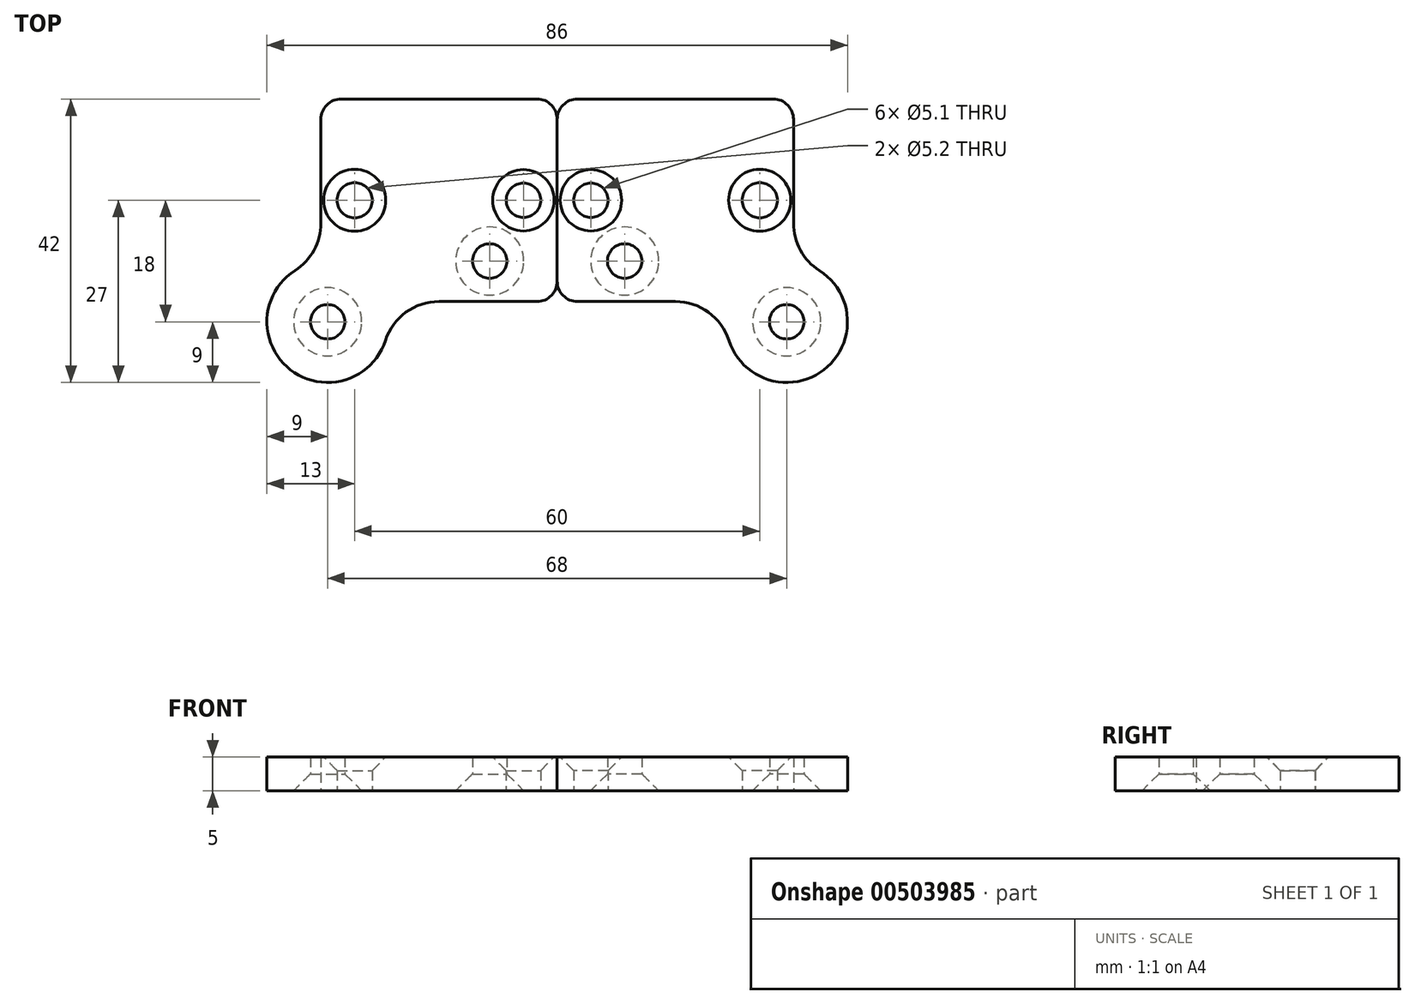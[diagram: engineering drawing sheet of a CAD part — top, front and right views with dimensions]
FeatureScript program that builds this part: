
annotation { "Feature Type Name" : "Feature", "Feature Type Description" : "" }
export const myFeature = defineFeature(function(context is Context, id is Id, definition is map)
    precondition{}
    {
        {
            var Q0;
            Q0=qCreatedBy(makeId("Top.planeOp"),FACE);
            var sketch = newSketch(context, id + "F0", { "sketchPlane" : qUnion([Q0])});
            skLineSegment(sketch, "E0", {"start": v(-17.5, -12) * mm, "end": v(-17.5, 12) * mm});
            skLineSegment(sketch, "E1", {"start": v(-14.5, 15) * mm, "end": v(14.5, 15) * mm});
            skCircle(sketch, "E2", {"center": v(-12.5, 0) * mm, "radius": 2.55 * mm});
            skLineSegment(sketch, "E3", {"start": v(-14.5, -15) * mm, "end": v(0, -15) * mm});
            skCircle(sketch, "E4", {"center": v(16.5, -18) * mm, "radius": 2.55 * mm});
            skLineSegment(sketch, "E5", {"start": v(-17.5, 0) * mm, "end": v(17.5, 0) * mm, "construction": true});
            skCircle(sketch, "E6", {"center": v(12.5, 0) * mm, "radius": 2.6 * mm});
            skLineSegment(sketch, "E7", {"start": v(0, 15) * mm, "end": v(0, -15) * mm, "construction": true});
            skPoint(sketch, "E8.visualSharp", {"position": v(-17.5, 15) * mm});
            skArc(sketch, "E8.filletArc", {"start": v(-14.5, 15) * mm, "mid": v(-16.62, 14.12) * mm, "end": v(-17.5, 12) * mm});
            skPoint(sketch, "E9.visualSharp", {"position": v(-17.5, -15) * mm});
            skArc(sketch, "E9.filletArc", {"start": v(-17.5, -12) * mm, "mid": v(-16.62, -14.12) * mm, "end": v(-14.5, -15) * mm});
            skCircle(sketch, "E10", {"center": v(-7.5, -9) * mm, "radius": 2.55 * mm});
            skLineSegment(sketch, "E11", {"start": v(17.5, 12) * mm, "end": v(17.5, -3.41) * mm});
            skCircle(sketch, "E12", {"center": v(16.5, -18) * mm, "radius": 9 * mm});
            skArc(sketch, "E13", {"start": v(7.94, -20.77) * mm, "mid": v(4.9, -16.6) * mm, "end": v(0, -15) * mm});
            skArc(sketch, "E14", {"start": v(17.5, -3.41) * mm, "mid": v(18.52, -7.4) * mm, "end": v(21.34, -10.41) * mm});
            skPoint(sketch, "E15.visualSharp", {"position": v(17.5, 15) * mm});
            skArc(sketch, "E15.filletArc", {"start": v(17.5, 12) * mm, "mid": v(16.62, 14.12) * mm, "end": v(14.5, 15) * mm});
            skSolve(sketch);
        }
        {
            var Q0;
            Q0=qSketchRegion(id+"F0",true);
            extrude(context, id + "F1", {"entities" : qUnion([Q0]), "depth" : 5 * mm, "offsetDistance" : 25 * mm});
        }
        {
            var Q0;
            Q0=makeQuery(id+"F1.opExtrude","CAP_EDGE",EDGE,{"disambiguationData":[OSD([sQuery(id+"F0.wireOp",EDGE,"E10")])],"isStart":true});
            chamfer(context, id + "F2", {"entities" : qUnion([Q0]), "width" : 2.5 * mm, "tangentPropagation" : true});
        }
        {
            var Q0;
            Q0=makeQuery(id+"F1.opExtrude","CAP_EDGE",EDGE,{"disambiguationData":[OSD([sQuery(id+"F0.wireOp",EDGE,"E6")])],"isStart":false});
            var Q1;
            Q1=makeQuery(id+"F1.opExtrude","CAP_EDGE",EDGE,{"disambiguationData":[OSD([sQuery(id+"F0.wireOp",EDGE,"E2")])],"isStart":false});
            chamfer(context, id + "F3", {"entities" : qUnion([Q0, Q1]), "width" : 2 * mm, "tangentPropagation" : true});
        }
        {
            var Q0;
            Q0=makeQuery(id+"F1.opExtrude","CAP_EDGE",EDGE,{"disambiguationData":[OSD([sQuery(id+"F0.wireOp",EDGE,"E4")])],"isStart":true});
            chamfer(context, id + "F4", {"entities" : qUnion([Q0]), "width" : 2.5 * mm, "tangentPropagation" : true});
        }
        {
            var Q0;
            Q0=makeQuery(id+"F1.opExtrude","SWEPT_BODY",BODY,{"disambiguationData":[OSD([sQuery(id+"F0.wireOp",EDGE,"E0"),sQuery(id+"F0.wireOp",EDGE,"E1"),sQuery(id+"F0.wireOp",EDGE,"kYZGjIat-fKnY-O7DV-UI95-udmZJz3vO766"),sQuery(id+"F0.wireOp",EDGE,"E2"),sQuery(id+"F0.wireOp",EDGE,"E3"),sQuery(id+"F0.wireOp",EDGE,"E4"),sQuery(id+"F0.wireOp",EDGE,"IHucLI0W-UAm1-2RkW-EwwA-VK9AypabfHPI"),sQuery(id+"F0.wireOp",EDGE,"E6"),sQuery(id+"F0.wireOp",EDGE,"KcrSqW35-f93I-OFAf-4m79-4XsPxfBBurTz"),sQuery(id+"F0.wireOp",EDGE,"0PqGULpz-Jk7b-MhiQ-okmd-zZGYFV39mjKV"),sQuery(id+"F0.wireOp",EDGE,"AEbkrw7Q-ej84-nH2O-E5ma-w5oqfJvolAAK"),sQuery(id+"F0.wireOp",EDGE,"E8.filletArc"),sQuery(id+"F0.wireOp",EDGE,"7f41deb0-f3f0-45c9-b0d4-537c99779641.filletArc"),sQuery(id+"F0.wireOp",EDGE,"E9.filletArc")])]});
            var Q1;
            Q1=makeQuery(id+"F1.opExtrude","SWEPT_FACE",FACE,{"disambiguationData":[OSD([sQuery(id+"F0.wireOp",EDGE,"E0")])]});
            mirror(context, id + "F5", {"entities" : qUnion([Q0]), "mirrorPlane" : qUnion([Q1])});
        }
    });
